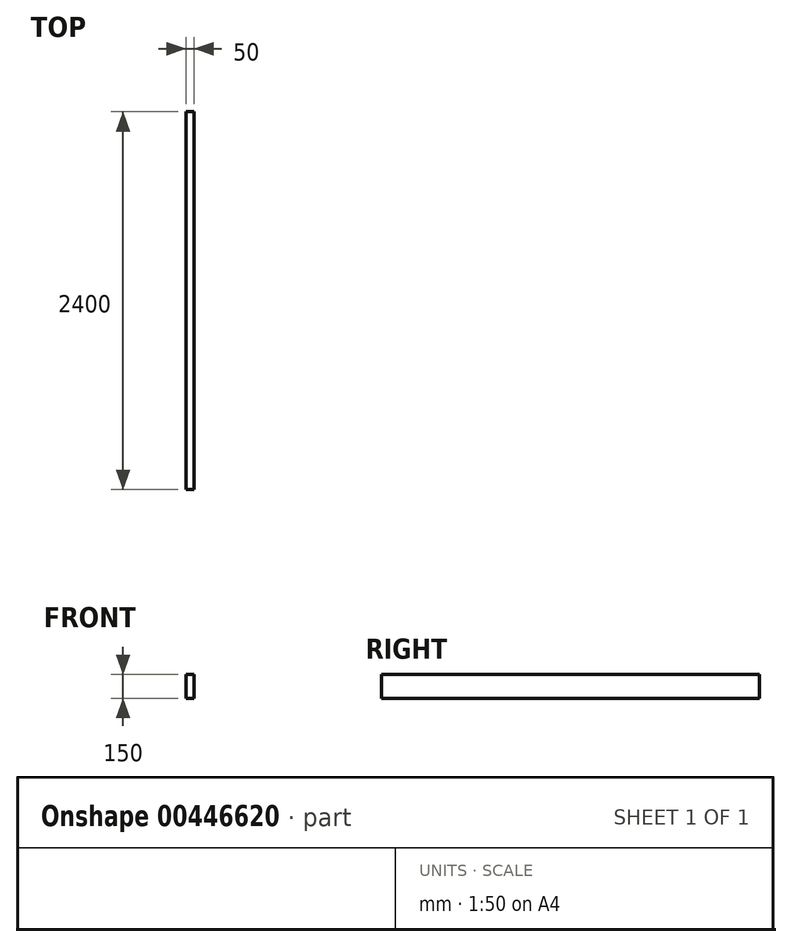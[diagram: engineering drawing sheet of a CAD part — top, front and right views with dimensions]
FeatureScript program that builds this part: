
annotation { "Feature Type Name" : "Feature", "Feature Type Description" : "" }
export const myFeature = defineFeature(function(context is Context, id is Id, definition is map)
    precondition{}
    {
        {
            var Q0;
            Q0=qCreatedBy(makeId("Front.planeOp"),FACE);
            var sketch = newSketch(context, id + "F0", { "sketchPlane" : qUnion([Q0])});
            skLineSegment(sketch, "E0.bottom", {"start": v(25, -75) * mm, "end": v(-25, -75) * mm});
            skLineSegment(sketch, "E0.top", {"start": v(25, 75) * mm, "end": v(-25, 75) * mm});
            skLineSegment(sketch, "E0.left", {"start": v(25, -75) * mm, "end": v(25, 75) * mm});
            skLineSegment(sketch, "E0.right", {"start": v(-25, -75) * mm, "end": v(-25, 75) * mm});
            skPoint(sketch, "E0.middle", {"position": v(0, 0) * mm});
            skSolve(sketch);
        }
        {
            var Q0;
            Q0=makeQuery(id+"F0.imprint","IMPRINT",FACE,{"disambiguationData":[TD([[makeQuery(id+"F0.imprint","IMPRINT",EDGE,{"derivedFrom":sQuery(id+"F0.wireOp",EDGE,"E0.bottom")}),-1.0]])]});
            extrude(context, id + "F1", {"entities" : qUnion([Q0]), "depth" : 2400 * mm});
        }
    });
